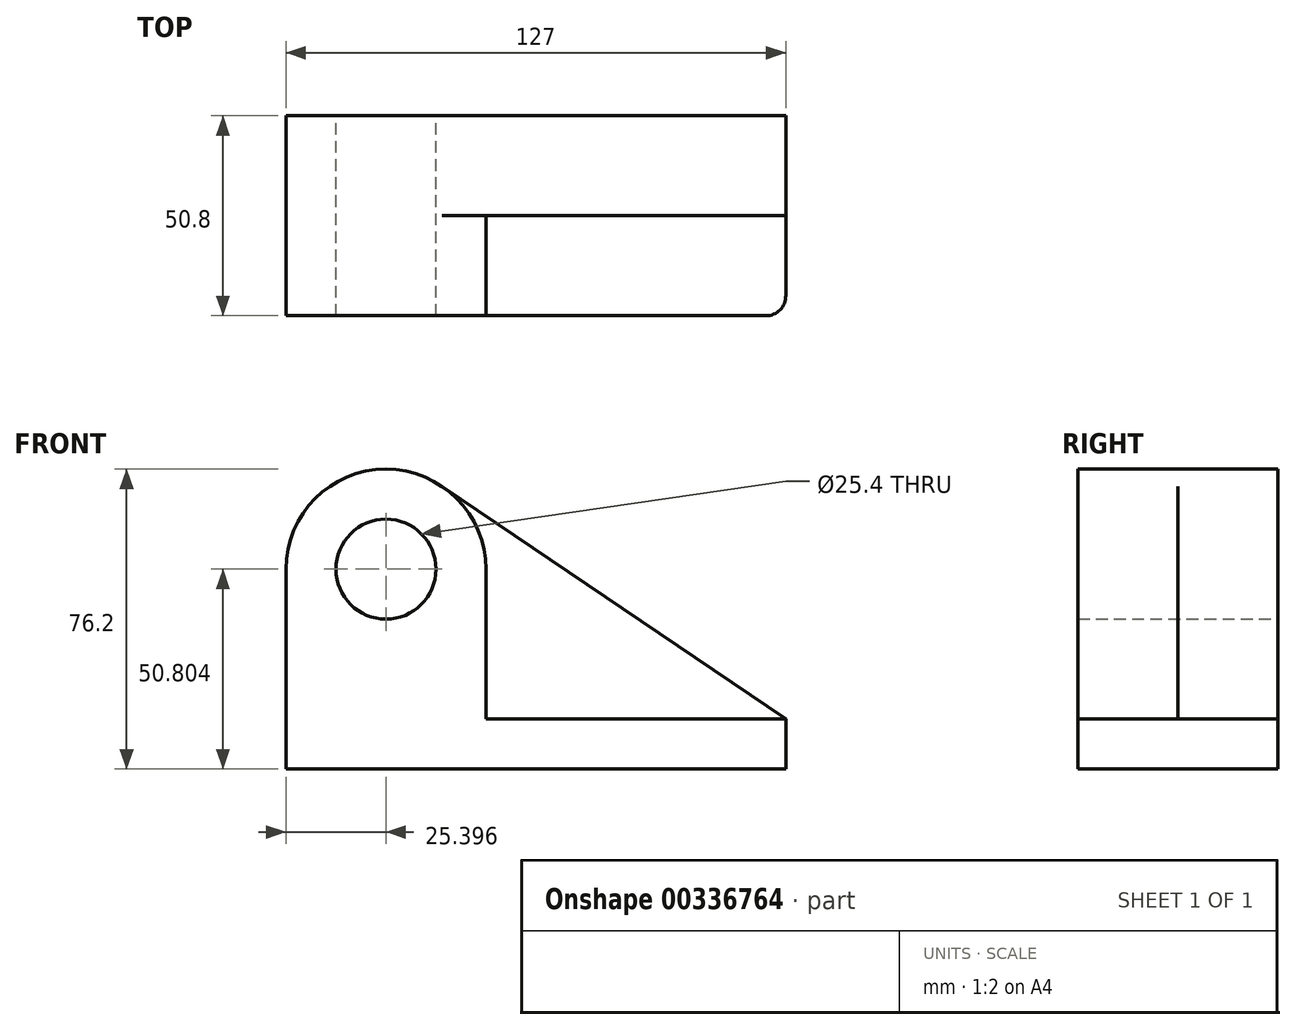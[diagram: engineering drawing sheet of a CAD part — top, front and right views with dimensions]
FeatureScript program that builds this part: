
annotation { "Feature Type Name" : "Feature", "Feature Type Description" : "" }
export const myFeature = defineFeature(function(context is Context, id is Id, definition is map)
    precondition{}
    {
        {
            var Q0;
            Q0=qCreatedBy(makeId("Front.planeOp"),FACE);
            var sketch = newSketch(context, id + "F0", { "sketchPlane" : qUnion([Q0])});
            skArc(sketch, "E0", {"start": v(-22.75, 60.5) * mm, "mid": v(-48.9, 61.9) * mm, "end": v(-62.38, 39.46) * mm});
            skCircle(sketch, "E1", {"center": v(-36.98, 39.46) * mm, "radius": 12.7 * mm});
            skLineSegment(sketch, "E2", {"start": v(-62.38, 39.46) * mm, "end": v(-62.38, -11.34) * mm});
            skLineSegment(sketch, "E3", {"start": v(-62.38, -11.34) * mm, "end": v(64.62, -11.34) * mm});
            skLineSegment(sketch, "E4", {"start": v(64.62, -11.34) * mm, "end": v(64.62, 1.36) * mm});
            skLineSegment(sketch, "E5", {"start": v(64.62, 1.36) * mm, "end": v(-22.75, 60.5) * mm});
            skSolve(sketch);
        }
        {
            var Q0;
            Q0=makeQuery(id+"F0.imprint","IMPRINT",FACE,{"disambiguationData":[TD([[makeQuery(id+"F0.imprint","IMPRINT",EDGE,{"derivedFrom":sQuery(id+"F0.wireOp",EDGE,"E0")}),1.0]])]});
            extrude(context, id + "F1", {"entities" : qUnion([Q0]), "depth" : 25.4 * mm});
        }
        {
            var Q0;
            Q0=makeQuery(id+"F1.opExtrude","CAP_FACE",FACE,{"disambiguationData":[OSD([sQuery(id+"F0.wireOp",EDGE,"E0"),sQuery(id+"F0.wireOp",EDGE,"E1"),sQuery(id+"F0.wireOp",EDGE,"E2"),sQuery(id+"F0.wireOp",EDGE,"E3"),sQuery(id+"F0.wireOp",EDGE,"E4"),sQuery(id+"F0.wireOp",EDGE,"E5")])],"isStart":false});
            var sketch = newSketch(context, id + "F2", { "sketchPlane" : qUnion([Q0])});
            skCircle(sketch, "E6", {"center": v(-36.98, 39.46) * mm, "radius": 12.7 * mm});
            skArc(sketch, "E7", {"start": v(-11.58, 39.46) * mm, "mid": v(-36.98, 64.86) * mm, "end": v(-62.38, 39.46) * mm});
            skLineSegment(sketch, "E8.bottom", {"start": v(64.62, 1.36) * mm, "end": v(-11.58, 1.36) * mm});
            skLineSegment(sketch, "E8.top", {"start": v(64.62, -11.34) * mm, "end": v(-62.38, -11.34) * mm});
            skLineSegment(sketch, "E8.left", {"start": v(64.62, 1.36) * mm, "end": v(64.62, -11.34) * mm});
            skLineSegment(sketch, "E8.right", {"start": v(-62.38, 1.36) * mm, "end": v(-62.38, -11.34) * mm});
            skLineSegment(sketch, "E9", {"start": v(-11.58, 39.46) * mm, "end": v(-11.58, 1.36) * mm});
            skLineSegment(sketch, "E10", {"start": v(-62.38, 39.46) * mm, "end": v(-62.38, 1.36) * mm});
            skSolve(sketch);
        }
        {
            var Q0;
            Q0=makeQuery(id+"F2.imprint","IMPRINT",FACE,{"disambiguationData":[TD([[makeQuery(id+"F2.imprint","IMPRINT",EDGE,{"derivedFrom":sQuery(id+"F2.wireOp",EDGE,"E6")}),-1.0]])]});
            extrude(context, id + "F3", {"entities" : qUnion([Q0]), "operationType" : NewBodyOperationType.ADD, "depth" : 25.4 * mm});
        }
        {
            var Q0;
            Q0=makeQuery(id+"F3.opExtrude","CAP_EDGE",EDGE,{"disambiguationData":[OSD([sQuery(id+"F2.wireOp",EDGE,"E8.left")])],"isStart":false});
            fillet(context, id + "F4", {"entities" : qUnion([Q0]), "radius" : 5.08 * mm, "tangentPropagation" : true, "allowEdgeOverflow" : false});
        }
    });
